# Revit family: PRD_AR_Snks_MaximaCommercialSink_MAXS112-140,MAXS117-140
name_source: partatom
category: Plumbing Fixtures
revit_build: Autodesk Revit 2018 (Build: 20190510_1515(x64)
units: mm (PartAtom-declared; Revit-internal decimal feet)

## family parameters
Always vertical = Yes
Cut with Voids When Loaded = No
OmniClass Number = 23.45.05.14.14
OmniClass Title = Sinks/Lavatories
Part Type = Normal
Room Calculation Point = No
Round Connector Dimension = Use Diameter
Shared = No
Work Plane-Based = No

## types (2) — shared parameters
Accessories = Shelf
AssetType = Fixed
BracketsMaterial = PRD_AR_StainlessSteel_SatinFinished
Category = Pr_40_20_96_45, Kitchen sinks
Color = stainless steel
Constituents = Underframe MAXF140-60
ConstructionFrameAssembly = Underframe to screw with Franke commercial sink
ConstructionFrameFinish = satin finished
ConstructionFrameMaterial = Square tubular leg frame, stainless steel 1.4301
DrainSize = DN 40 (1 1/2 inch.)
DurationUnit = year
Features = stainless steel, 1.00 mm, satin finished
Finish = satin finished
GrossWeight = 17.50 kg
IfcExportAs = IfcSanitaryTerminalType
IfcExportType = SINK
Manufacturer = KWC Group AG
ManufacturerName = KWC Group AG
ManufacturerURL = www.kwc.com
Material = stainless steel
MaterialCode = stainless steel 1.4301
NBSDescription = Commercial stainless steel sinks
NBSReference = 45-35-15/432
NetWeight = 14.50 kg
NominalDepth = 600 mm  [stored 1.9685 ft]
NominalHeight = 432 mm  [stored 1.41732 ft]
NominalWidth = 1400 mm  [stored 4.59318 ft]
OverallDimensionsDepthMaximum = 600 mm  [stored 1.9685 ft]
OverallDimensionsHeightMaximum = 1000 mm  [stored 3.28084 ft]
OverallDimensionsLengthMaximum = 1400 mm  [stored 4.59318 ft]
ProductInformation = https://pim.kwc.com
Shape = Rectangular
SinkMaterial = PRD_AR_StainlessSteel_SatinFinished
SinkMounting = Other
SinkType = Rinsing
Size = 1400 x 432 x 600 mm
URL = www.kwc.com
UnderframeMaterial = PRD_AR_StainlessSteel_SatinFinished
Uniclass2015Code = Pr_40_20_96_45
Uniclass2015Title = Kitchen sinks
Uniclass2015Version = Products v1.10
Version = 1
WarrantyDurationUnit = year
WashBowlsDepthMaximum = 300 mm
WashBowlsLengthMaximum = 500 mm  [stored 1.64042 ft]
WashBowlsTapArrangement = 80 mm tap ledge
WashBowlsWasteDiameter = DN 40 (1 1/2 inch.)
WashBowlsWasteMaterial = stainless steel
WashBowlsWidthMaximum = 400 mm  [stored 1.31234 ft]
WasteSize = 40  [stored 0.131234 ft]

## per-type parameters (varying)
| type | Arrangement | BIMObjectName | Description | LeftDrainBoard | ModelNumber | Name | RightDrainBoard | WashBowlsWasteArrangement |
| MAXS112-140 | One bowl sink with relief pattern right hand drainer | PRD_AR_KitchenSinks_MaximaCommercialSink_MAXS112-140 | Commercial sink for inset or wall mounting, stainless steel, surface satin finished, material thickness 1 mm, deep drawn seamless welded bowl with dimensions, without overflow and 80 mm tap ledge, bowl left or right, 1 1/2" waste with two part overflow tube consisting of perforated stainless steel tube and plastic tube, drain board with riffle and slanted to bowl, drain board with reinforced stainless steel bracket, 100 mm rear upstand, wall mounting brackets optional, drilling holes for wall mounting prelasered.
Drain board right | No | 2000057662 | Maxima catering sink MAXS112-140 | Yes | Right-Back-Corner |
| MAXS117-140 | One bowl sink with relief pattern left hand drainer | PRD_AR_KitchenSinks_MaximaCommercialSinkSet_MAXS117-140 | Commercial sink for inset or wall mounting, stainless steel, surface satin finished, material thickness 1 mm, deep drawn seamless welded bowl with dimensions, without overflow and 80 mm tap ledge, bowl left or right, 1 1/2" waste with two part overflow tube consisting of perforated stainless steel tube and plastic tube, drain board with riffle and slanted to bowl, drain board with reinforced stainless steel bracket, 100 mm rear upstand, wall mounting brackets optional, drilling holes for wall mounting prelasered.
Drain board left | Yes | 2000057700 | Maxima catering sink MAXS117-140 | No | Left-Back-Corner |

note: column(s) folded — value = type name in every type: Model, ModelReference

note: [stored X ft] marks values corroborated as IEEE doubles in the binary element streams (Revit-internal decimal feet)

## geometry (parser evidence)
native form markers: Sweep x10
no freeform markers — native parametric forms only
